# Revit family: NU-620
name_source: partatom
category: Mechanical Equipment
revit_build: Autodesk Revit 2018 (Build: 20180423_1000(x64)
units: mm (PartAtom-declared; Revit-internal decimal feet)

## family parameters
Always vertical = Yes
Cut with Voids When Loaded = No
OmniClass Number = 23.75.00.00
OmniClass Title = Climate Control (HVAC)
Part Type = Normal
Room Calculation Point = No
Round Connector Dimension = Use Diameter
Shared = No
Work Plane-Based = No

## types (3) — shared parameters
DEPTH = 2' - 6 1/2"
HEIGHT = 7' - 8 21/32"
Manufacturer = NuAire Inc.

## per-type parameters (varying)
| type | Description | Model | Type Comments | WIDTH |
| NU-620-400 | 4 ft.  SMALL ANIMAL CAGE CHANGING STATION | NU-S620-400M | (Innovive model number) | 4' - 0 1/8" |
| NU-620-500 | 5 ft.  SMALL ANIMAL CAGE CHANGING STATION | NU-S620-500M/R | (Innovive model numbers) | 5' - 0 3/4" |
| NU-620-300 | 3 ft.  SMALL ANIMAL CAGE CHANGING STATION | NU-620-300 |  | 3' - 6 1/8" |

## geometry (parser evidence)
native form markers: Blend x13, Sweep x2
no freeform markers — native parametric forms only
